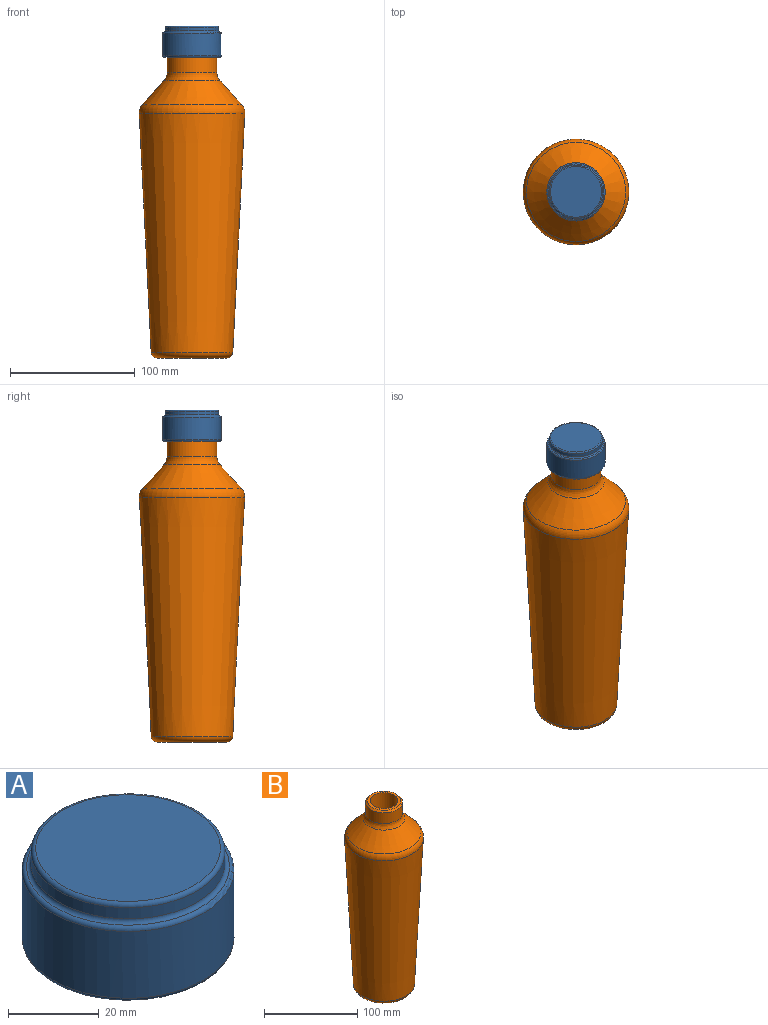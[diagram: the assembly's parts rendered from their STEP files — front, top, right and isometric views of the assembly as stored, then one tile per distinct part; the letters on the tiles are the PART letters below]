
ASSEMBLY  parts=2 mates=1
PART A: 14 faces, bbox 50.6x50.6x25 mm
  f0: plane 38.72x38.72mm, normal (0,0,-1), area 1177.2mm2, adj f1
  f1: cylinder r=19.36mm len=38.72mm, axis (0,0,-1), area 608.1mm2, adj f0,f2
  f2: plane 42.72x42.72mm, normal (0,0,-1), area 255.8mm2, adj f1,f3
  f3: cylinder r=21.36mm len=42.72mm, axis (0,0,-1), area 2147.1mm2, adj f2,f4
  f4: plane 42.72x42.72mm, normal (0,0,1), area 191.7mm2, adj f3,f5
  f5: cylinder r=19.88mm len=39.76mm, axis (0,0,-1), area 249.8mm2, adj f4,f6
  f6: plane 44.72x44.72mm, normal (0,0,-1), area 329mm2, adj f5,f10
  f7: cylinder r=23.36mm len=46.72mm, axis (0,0,-1), area 2641.7mm2, adj f10,f12
  f8: cylinder r=21.36mm len=42.72mm, axis (0,0,-1), area 402.6mm2, adj f11,f13
  f9: plane 40.72x40.72mm, normal (0,0,1), area 1302mm2, adj f13
  f10: torus R=22.36mm, axis (0,0,-1), area 226.9mm2, adj f6,f7
  f11: torus R=22.36mm, axis (0,0,1), area 214.4mm2, adj f8,f12
  f12: torus R=22.36mm, axis (0,0,1), area 226.9mm2, adj f7,f11
  f13: torus R=20.36mm, axis (0,0,1), area 207.2mm2, adj f8,f9
PART B: 13 faces, bbox 91.6x91.6x245 mm
  f0: plane 35.76x35.76mm, normal (0,0,1), area 308.7mm2, adj f1,f12
  f1: cylinder r=14.88mm len=29.76mm, axis (0,0,-1), area 2049.7mm2, adj f0,f2
  f2: cone r=37.4mm half-angle=42.1deg, axis (0,0,-1), area 5513.4mm2, adj f1,f3
  f3: cone r=27.74mm half-angle=2.9deg, axis (0,0,1), area 39585.2mm2, adj f2,f4
  f4: plane 55.49x55.49mm, normal (0,0,1), area 2418.1mm2, adj f3
  f5: plane 55.49x55.49mm, normal (0,0,-1), area 2418.1mm2, adj f11
  f6: cone r=32.5mm half-angle=2.9deg, axis (0,0,1), area 45103.2mm2, adj f9,f11
  f7: cone r=42.5mm half-angle=42.1deg, axis (0,0,-1), area 5024.3mm2, adj f9,f10
  f8: cylinder r=19.88mm len=39.76mm, axis (0,0,-1), area 1767mm2, adj f10,f12
  f9: torus R=32.3mm, axis (0,0,1), area 2047mm2, adj f6,f7
  f10: torus R=29.88mm, axis (0,0,-1), area 959.1mm2, adj f7,f8
  f11: torus R=27.74mm, axis (0,0,-1), area 1474.8mm2, adj f5,f6
  f12: cone r=19.88mm half-angle=45deg, axis (0,0,-1), area 335.5mm2, adj f0,f8
PLACE A t=(0,0,-4)mm
PLACE B at identity fixed
MATE fastened A.f1 <-> B.f1  axis (0,0,1) through (0,0,243)mm
